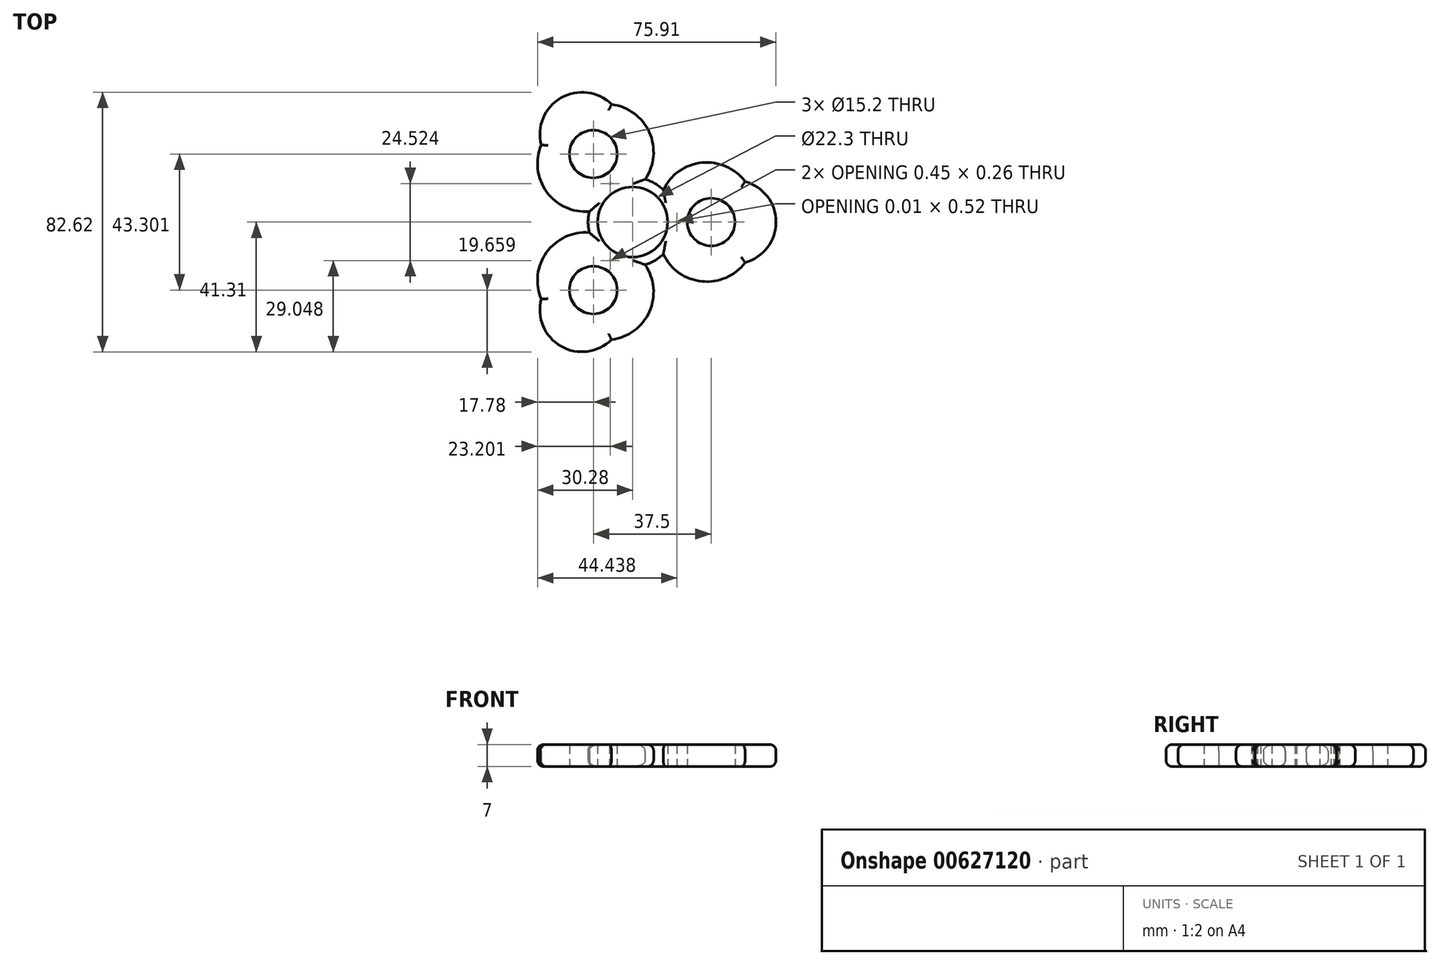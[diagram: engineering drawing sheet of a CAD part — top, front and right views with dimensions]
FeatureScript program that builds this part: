
annotation { "Feature Type Name" : "Feature", "Feature Type Description" : "" }
export const myFeature = defineFeature(function(context is Context, id is Id, definition is map)
    precondition{}
    {
        {
            var Q0;
            Q0=qCreatedBy(makeId("Top.planeOp"),FACE);
            var sketch = newSketch(context, id + "F0", { "sketchPlane" : qUnion([Q0])});
            skCircle(sketch, "E0", {"center": v(0, 0) * mm, "radius": 11.15 * mm});
            skCircle(sketch, "E1", {"center": v(25, 0) * mm, "radius": 7.6 * mm});
            skCircle(sketch, "E2", {"center": v(25, 0) * mm, "radius": 10.84 * mm});
            skCircle(sketch, "E3", {"center": v(0, 0) * mm, "radius": 14.16 * mm});
            skArc(sketch, "E4", {"start": v(35.8, 12.91) * mm, "mid": v(22.04, 18.9) * mm, "end": v(9.78, 10.24) * mm});
            skArc(sketch, "E5.MirrorCS", {"start": v(35.8, -12.91) * mm, "mid": v(22.04, -18.9) * mm, "end": v(9.78, -10.24) * mm});
            skArc(sketch, "E6", {"start": v(35.8, -12.91) * mm, "mid": v(45.63, 0) * mm, "end": v(35.8, 12.91) * mm});
            skArc(sketch, "E7.1.0", {"start": v(-29.08, 24.54) * mm, "mid": v(-27.38, 9.64) * mm, "end": v(-13.76, 3.35) * mm});
            skCircle(sketch, "E7.1.1", {"center": v(-12.5, 21.65) * mm, "radius": 10.84 * mm});
            skCircle(sketch, "E7.1.2", {"center": v(-12.5, 21.65) * mm, "radius": 7.6 * mm});
            skArc(sketch, "E7.1.3", {"start": v(-6.71, 37.46) * mm, "mid": v(-22.82, 39.52) * mm, "end": v(-29.08, 24.54) * mm});
            skArc(sketch, "E7.1.4", {"start": v(-6.71, 37.46) * mm, "mid": v(5.34, 28.53) * mm, "end": v(3.98, 13.6) * mm});
            skArc(sketch, "E7.2.0", {"start": v(-6.71, -37.46) * mm, "mid": v(5.34, -28.53) * mm, "end": v(3.98, -13.6) * mm});
            skCircle(sketch, "E7.2.1", {"center": v(-12.5, -21.65) * mm, "radius": 10.84 * mm});
            skCircle(sketch, "E7.2.2", {"center": v(-12.5, -21.65) * mm, "radius": 7.6 * mm});
            skArc(sketch, "E7.2.3", {"start": v(-29.08, -24.54) * mm, "mid": v(-22.82, -39.52) * mm, "end": v(-6.71, -37.46) * mm});
            skArc(sketch, "E7.2.4", {"start": v(-29.08, -24.54) * mm, "mid": v(-27.38, -9.64) * mm, "end": v(-13.76, -3.35) * mm});
            skSolve(sketch);
        }
        {
            var Q0;
            Q0 = qSketchRegion(id + "F0", true);
            var Q1;
            Q1=makeQuery(id+"F0.imprint","IMPRINT",FACE,{"disambiguationData":[TD([[makeQuery(id+"F0.imprint","IMPRINT",EDGE,{"derivedFrom":sQuery(id+"F0.wireOp",EDGE,"E7.1.2")}),-1.0]])]});
            var Q2;
            Q2=makeQuery(id+"F0.imprint","IMPRINT",FACE,{"disambiguationData":[TD([[makeQuery(id+"F0.imprint","IMPRINT",EDGE,{"derivedFrom":sQuery(id+"F0.wireOp",EDGE,"E7.2.2")}),-1.0]])]});
            var Q3;
            Q3=makeQuery(id+"F0.imprint","IMPRINT",FACE,{"disambiguationData":[TD([[makeQuery(id+"F0.imprint","IMPRINT",EDGE,{"derivedFrom":sQuery(id+"F0.wireOp",EDGE,"E1")}),-1.0]])]});
            extrude(context, id + "F1", {"entities" : qUnion([Q0, Q1, Q2, Q3]), "depth" : 7 * mm, "offsetDistance" : 25 * mm});
        }
        {
            var Q0;
            Q0=makeQuery(id+"F1.opExtrude","CAP_EDGE",EDGE,{"disambiguationData":[OSD([sQuery(id+"F0.wireOp",EDGE,"E7.1.4")])],"isStart":true});
            var Q1;
            Q1=makeQuery(id+"F1.opExtrude","CAP_EDGE",EDGE,{"disambiguationData":[OSD([sQuery(id+"F0.wireOp",EDGE,"E7.1.3")])],"isStart":true});
            var Q2;
            Q2=makeQuery(id+"F1.opExtrude","CAP_EDGE",EDGE,{"disambiguationData":[OSD([sQuery(id+"F0.wireOp",EDGE,"E7.1.0")])],"isStart":true});
            var Q3;
            Q3=makeQuery(id+"F1.opExtrude","CAP_EDGE",EDGE,{"disambiguationData":[OSD([sQuery(id+"F0.wireOp",EDGE,"E4")])],"isStart":true});
            var Q4;
            Q4=makeQuery(id+"F1.opExtrude","CAP_EDGE",EDGE,{"disambiguationData":[OSD([sQuery(id+"F0.wireOp",EDGE,"E6")])],"isStart":true});
            var Q5;
            Q5=makeQuery(id+"F1.opExtrude","CAP_EDGE",EDGE,{"disambiguationData":[OSD([sQuery(id+"F0.wireOp",EDGE,"E5.MirrorCS")])],"isStart":true});
            var Q6;
            Q6=makeQuery(id+"F1.opExtrude","CAP_EDGE",EDGE,{"disambiguationData":[OSD([sQuery(id+"F0.wireOp",EDGE,"E7.2.0")])],"isStart":true});
            var Q7;
            Q7=makeQuery(id+"F1.opExtrude","CAP_EDGE",EDGE,{"disambiguationData":[OSD([sQuery(id+"F0.wireOp",EDGE,"E7.2.4")])],"isStart":true});
            var Q8;
            Q8=makeQuery(id+"F1.opExtrude","CAP_EDGE",EDGE,{"disambiguationData":[OSD([sQuery(id+"F0.wireOp",EDGE,"E7.2.3")])],"isStart":true});
            var Q9;
            {var subQ0=sQuery(id+"F0.wireOp",EDGE,"E3");Q9=makeQuery(id+"F1.opExtrude","CAP_EDGE",EDGE,{"disambiguationData":[OSD([subQ0]),TDD([makeQuery(id+"F0.imprint","IMPRINT",EDGE,{"disambiguationData":[TD([[makeQuery(id+"F0.imprint","INTERSECT",VERTEX,{"derivedFrom":[subQ0,sQuery(id+"F0.wireOp",EDGE,"E4")]}),-1.0]])],"derivedFrom":subQ0})])],"isStart":true});}
            var Q10;
            {var subQ0=sQuery(id+"F0.wireOp",EDGE,"E3");Q10=makeQuery(id+"F1.opExtrude","CAP_EDGE",EDGE,{"disambiguationData":[OSD([subQ0]),TDD([makeQuery(id+"F0.imprint","IMPRINT",EDGE,{"disambiguationData":[TD([[makeQuery(id+"F0.imprint","INTERSECT",VERTEX,{"derivedFrom":[subQ0,sQuery(id+"F0.wireOp",EDGE,"E7.1.0")]}),-1.0]])],"derivedFrom":subQ0})])],"isStart":true});}
            var Q11;
            {var subQ0=sQuery(id+"F0.wireOp",EDGE,"E3");Q11=makeQuery(id+"F1.opExtrude","CAP_EDGE",EDGE,{"disambiguationData":[OSD([subQ0]),TDD([makeQuery(id+"F0.imprint","IMPRINT",EDGE,{"disambiguationData":[TD([[makeQuery(id+"F0.imprint","INTERSECT",VERTEX,{"derivedFrom":[subQ0,sQuery(id+"F0.wireOp",EDGE,"E5.MirrorCS")]}),1.0]])],"derivedFrom":subQ0})])],"isStart":true});}
            var Q12;
            Q12=makeQuery(id+"F1.opExtrude","CAP_EDGE",EDGE,{"disambiguationData":[OSD([sQuery(id+"F0.wireOp",EDGE,"E7.2.4")])],"isStart":false});
            var Q13;
            Q13=makeQuery(id+"F1.opExtrude","CAP_EDGE",EDGE,{"disambiguationData":[OSD([sQuery(id+"F0.wireOp",EDGE,"E7.2.3")])],"isStart":false});
            var Q14;
            Q14=makeQuery(id+"F1.opExtrude","CAP_EDGE",EDGE,{"disambiguationData":[OSD([sQuery(id+"F0.wireOp",EDGE,"E7.2.0")])],"isStart":false});
            var Q15;
            {var subQ0=sQuery(id+"F0.wireOp",EDGE,"E3");Q15=makeQuery(id+"F1.opExtrude","CAP_EDGE",EDGE,{"disambiguationData":[OSD([subQ0]),TDD([makeQuery(id+"F0.imprint","IMPRINT",EDGE,{"disambiguationData":[TD([[makeQuery(id+"F0.imprint","INTERSECT",VERTEX,{"derivedFrom":[subQ0,sQuery(id+"F0.wireOp",EDGE,"E5.MirrorCS")]}),1.0]])],"derivedFrom":subQ0})])],"isStart":false});}
            var Q16;
            Q16=makeQuery(id+"F1.opExtrude","CAP_EDGE",EDGE,{"disambiguationData":[OSD([sQuery(id+"F0.wireOp",EDGE,"E5.MirrorCS")])],"isStart":false});
            var Q17;
            Q17=makeQuery(id+"F1.opExtrude","CAP_EDGE",EDGE,{"disambiguationData":[OSD([sQuery(id+"F0.wireOp",EDGE,"E6")])],"isStart":false});
            var Q18;
            Q18=makeQuery(id+"F1.opExtrude","CAP_EDGE",EDGE,{"disambiguationData":[OSD([sQuery(id+"F0.wireOp",EDGE,"E4")])],"isStart":false});
            var Q19;
            Q19=makeQuery(id+"F1.opExtrude","CAP_EDGE",EDGE,{"disambiguationData":[OSD([sQuery(id+"F0.wireOp",EDGE,"E7.1.4")])],"isStart":false});
            var Q20;
            Q20=makeQuery(id+"F1.opExtrude","CAP_EDGE",EDGE,{"disambiguationData":[OSD([sQuery(id+"F0.wireOp",EDGE,"E7.1.3")])],"isStart":false});
            var Q21;
            Q21=makeQuery(id+"F1.opExtrude","CAP_EDGE",EDGE,{"disambiguationData":[OSD([sQuery(id+"F0.wireOp",EDGE,"E7.1.0")])],"isStart":false});
            var Q22;
            {var subQ0=sQuery(id+"F0.wireOp",EDGE,"E3");Q22=makeQuery(id+"F1.opExtrude","CAP_EDGE",EDGE,{"disambiguationData":[OSD([subQ0]),TDD([makeQuery(id+"F0.imprint","IMPRINT",EDGE,{"disambiguationData":[TD([[makeQuery(id+"F0.imprint","INTERSECT",VERTEX,{"derivedFrom":[subQ0,sQuery(id+"F0.wireOp",EDGE,"E7.1.0")]}),-1.0]])],"derivedFrom":subQ0})])],"isStart":false});}
            var Q23;
            {var subQ0=sQuery(id+"F0.wireOp",EDGE,"E3");Q23=makeQuery(id+"F1.opExtrude","CAP_EDGE",EDGE,{"disambiguationData":[OSD([subQ0]),TDD([makeQuery(id+"F0.imprint","IMPRINT",EDGE,{"disambiguationData":[TD([[makeQuery(id+"F0.imprint","INTERSECT",VERTEX,{"derivedFrom":[subQ0,sQuery(id+"F0.wireOp",EDGE,"E4")]}),-1.0]])],"derivedFrom":subQ0})])],"isStart":false});}
            fillet(context, id + "F2", {"entities" : qUnion([Q0, Q1, Q2, Q3, Q4, Q5, Q6, Q7, Q8, Q9, Q10, Q11, Q12, Q13, Q14, Q15, Q16, Q17, Q18, Q19, Q20, Q21, Q22, Q23]), "radius" : 2 * mm, "tangentPropagation" : true, "allowEdgeOverflow" : false});
        }
    });
